# Revit family: EIHLS-L-424-800-840x
name_source: partatom
category: Leuchten
revit_build: Autodesk Revit 2017 (Build: 20190508_0315(x64)
units: mm (PartAtom-declared; Revit-internal decimal feet)

## family parameters
Basisbauteil = Fläche
Beim Laden mit Abzugskörper schneiden = Nein
Bemaßung runder Anschluss = Durchmesser verwenden
Gemeinsam genutzt = Nein
Lichtquelle = Ja
OmniClass-Nummer = 23.80.70.11
OmniClass-Titel = Luminaries for Internal Lighting
Raumberechnungspunkt = Nein
Teiletyp = Normal

## types (8) — shared parameters
Baugruppenkennzeichen = D5020200
Emissionsform beim Rendern sichtbar = Nein
Farbfilter = 16777215
Farbtemperaturverschiebung bei Dämpfen der Lampe = <Keine Auswahl>
Hersteller = RIDI Leuchten GmbH
Lampe = LED
Neigungswinkel = 90.00°
Scheinlast = 61 VA
URL = www.ridi.de
Von Breite des Rechtecks ausssenden = 572 mm
Von Länge des Rechtecks aussenden = 572 mm
brand = RIDI
conformity mark = CE
electrical safety class = 1
height = 89 mm  [stored 0.291995 ft]
ingress protection (IP) code = IP64
length = 624 mm  [stored 2.04724 ft]
nominal frequency = 50-60Hz
nominal voltage = 230
rated input power = 61
voltage type (AC, DC, UC) = AC
weight = 9,9 kg
width = 624 mm  [stored 2.04724 ft]
zero-valued in all types: Vorgabe-Ansicht

## per-type parameters (varying)
| type | Datei für fotometrisches Netz | Modell |
| EIHLS-L 424/800-840 SM | EIHLS-L 4541640-840 SM.IES | 0850589 |
| EIHLS-L 424/800-840 SM-DA | EIHLS-L 4541640-840 SM.IES | 0860589 |
| EIHLS-L 424/800-840 SB | EIHLS-L 4541640-840 SB.IES | 0850461 |
| EIHLS-L 424/800-840 SB-DA | EIHLS-L 4541640-840 SB.IES | 0860461 |
| EIHLS-L 424/800-840 OS | EIHLS-L 4541640-840-OS.IES | 0850471 |
| EIHLS-L 424/800-840 OS-DA | EIHLS-L 4541640-840-OS.IES | 0860471 |
| EIHLS-L 424/800-840 W | EIHLS-L 4541640-840 W.IES | 0850481 |
| EIHLS-L 424/800-840 W-DA | EIHLS-L 4541640-840 W.IES | 0860481 |

note: column(s) folded — value = type name in every type: product name

note: [stored X ft] marks values corroborated as IEEE doubles in the binary element streams (Revit-internal decimal feet)
